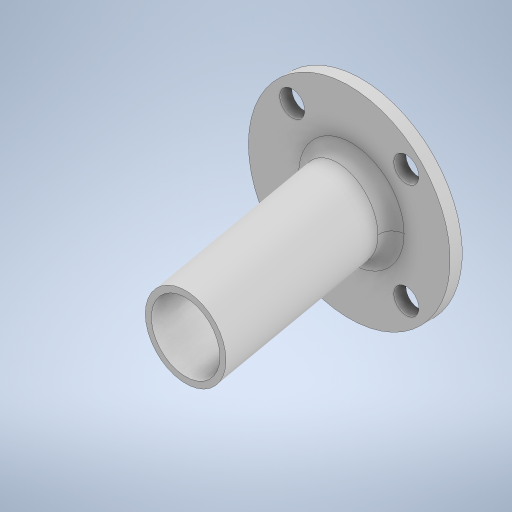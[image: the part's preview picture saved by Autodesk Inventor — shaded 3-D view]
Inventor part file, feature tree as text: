
AUTODESK INVENTOR PART (.ipt)
format: ipt  version: 2023 (Build 270158000, 158)  size: 316,416 bytes
history: native  units: in
note: dims shown in document units (in); Inventor stores cm internally (conversion verified against a paired STEP export)
features: sketch x5, sweep x2, extrude x1, fillet x1
ambient origin geometry x8: Origin, YZ Plane, XZ Plane, XY Plane, X Axis, Y Axis, Z Axis, Center Point
bodies: Solid1 (feature_tree)
feature tree (9):
  extrude  "Extrusion1"  Depth=0.2461in
  sweep  "Sweep4"
  sweep  "Sweep5"
  fillet  "Fillet2"  Radius=0.7874in
  sketch  "Sketch2"  dims[d0=1.9685in d10=0.2461in]
  sketch  "Sketch19"  dims[d11=0.2461in d12=0.2461in]
  sketch  "Sketch22"  dims[d13=0.2461in d14=0.1181in d15=0.0in d40=0.7874in]
  sketch  "Sketch23"  dims[d41=1.9685in]
  sketch  "Sketch25"  dims[d42=0.6871in d43=0.0in d44=0.0in d45=0.6693in d46=1.9685in d47=0.6871in d48=0.0in d49=0.0in d50=0.1181in]
